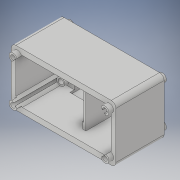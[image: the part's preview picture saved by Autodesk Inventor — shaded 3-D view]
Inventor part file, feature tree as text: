
AUTODESK INVENTOR PART (.ipt)
format: ipt  version: 2019 (Build 230136000, 136)  size: 378,368 bytes
history: native  units: mm
features: extrude x16, sketch x9, projected_geometry x3, other x3, fillet x2, reference x2
ambient origin geometry x8: Origin, YZ Plane, XZ Plane, XY Plane, X Axis, Y Axis, Z Axis, Center Point
bodies: Solid1 (feature_tree)
feature tree (35):
  sketch  "Sketch1"  dims[d0=22.75mm d1=12.2mm d2=9.0mm]
  extrude  "Extrusion1"  Depth=12.2mm
  fillet  "Fillet1"  Radius=9.0mm
  extrude  "Extrusion2"  Depth=1.0mm
  extrude  "Extrusion3"  Depth=10.5mm TaperAngle=0.0deg
  extrude  "Extrusion6"  Depth=1.0mm TaperAngle=0.0deg
  fillet  "Fillet2"  Radius=1.0mm
  sketch  "Sketch3"  dims[d6=1.75mm d7=10.5mm d8=0.0mm]
  extrude  "Extrusion7"  Depth=1.0mm
  sketch  "Sketch4"  dims[d9=1.0mm d10=1.0mm d11=0.0mm d12=1.0mm d13=0.0mm]
  extrude  "Extrusion9"  Depth=1.4mm
  extrude  "Extrusion10"  Depth=1.4mm
  extrude  "Extrusion15"  Depth=1.4mm
  extrude  "Extrusion16"  Depth=0.01mm
  sketch  "Sketch8"  dims[d19=1.4mm d20=1.4mm]
  extrude  "Extrusion17"  Depth=1.4mm
  extrude  "Extrusion18"  Depth=1.4mm
  extrude  "Extrusion19"  Depth=0.75mm
  extrude  "Extrusion20"  Depth=12.0mm
  sketch  "Sketch9"  dims[d21=1.4mm d22=1.4mm]
  extrude  "Extrusion21"  Depth=7.0mm
  extrude  "Extrusion22"  Depth=0.25mm
  extrude  "Extrusion23"  Depth=2.0mm
  sketch  "Sketch2"  dims[d3=20.0mm d4=1.0mm]
  projected_geometry  "Projected Loop1"
  sketch  "Sketch6"  dims[d15=1.2mm d16=1.0mm]
  reference  "Reference1"
  reference  "Reference2"
  sketch  "Sketch7"  dims[d17=1.4mm d18=1.4mm]
  projected_geometry  "Projected Loop2"
  sketch  "Sketch10"  dims[d27=2.0mm d28=9.0mm d29=0.0mm d30=0.0mm d31=0.01mm d32=1.4mm d33=1.4mm d34=0.75mm d35=12.0mm d36=7.0mm d37=0.25mm d38=2.0mm d39=1.025mm d40=6.5mm d41=0.0mm d44=1.0mm d45=0.0mm d46=0.75mm d47=0.75mm d48=2.0mm d49=3.5mm d50=4.75mm d51=2.0mm d52=0.0mm d59=1.25mm d60=2.5mm d65=0.25mm d66=0.0mm d67=2.0mm d68=0.0mm d69=1.15mm d70=2.0mm d71=0.5mm d72=0.0mm d73=0.25mm d74=0.0mm d75=4.0mm d77=4.75mm d78=0.75mm d79=0.0mm d80=0.75mm d81=0.0mm d82=5.0mm d83=6.0mm d84=1.0mm d85=0.0mm d86=8.0mm d89=2.75mm d90=1.75mm d91=1.0mm d92=0.0mm d93=1.0mm d94=0.0mm d95=2.25mm d96=1.15mm d97=10.75mm d98=10.0mm d99=0.0mm]
  projected_geometry  "Projected Loop3"
  other  "<userpath>\OneDrive\Documenten\Inventor\servo\Assembly1.iam"
  other  "Assembly1.iam"
  other  "sevo boven:1"
